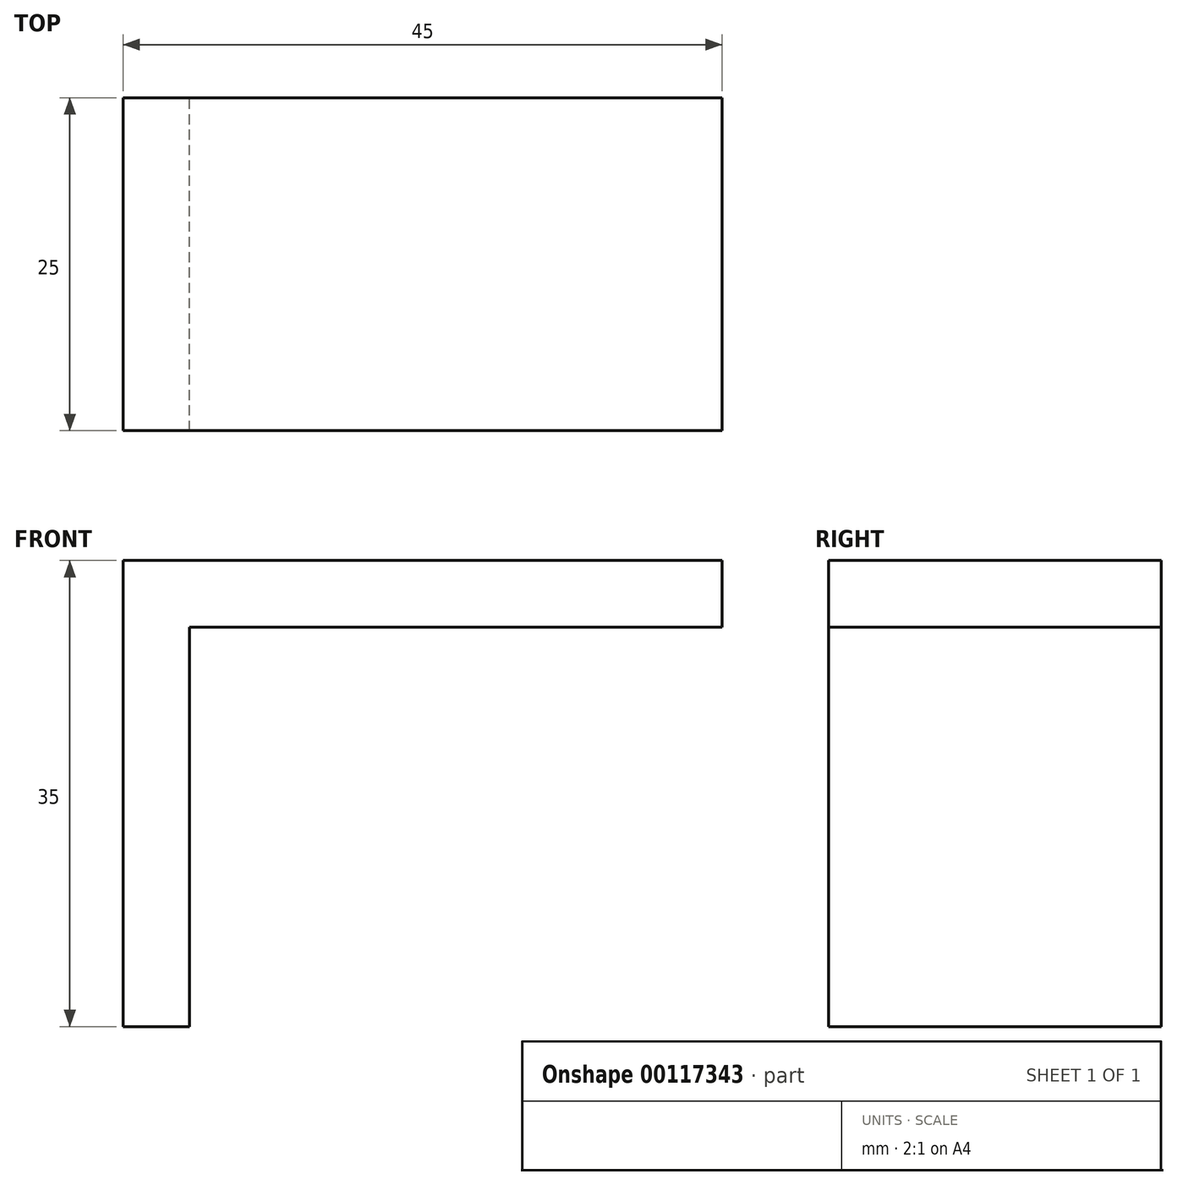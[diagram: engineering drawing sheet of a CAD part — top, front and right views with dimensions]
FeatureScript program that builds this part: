
annotation { "Feature Type Name" : "Feature", "Feature Type Description" : "" }
export const myFeature = defineFeature(function(context is Context, id is Id, definition is map)
    precondition{}
    {
        {
            var Q0;
            Q0=qCreatedBy(makeId("Front.planeOp"),FACE);
            var sketch = newSketch(context, id + "F0", { "sketchPlane" : qUnion([Q0])});
            skLineSegment(sketch, "E0", {"start": v(0, 0) * mm, "end": v(5, 0) * mm});
            skLineSegment(sketch, "E1", {"start": v(5, 0) * mm, "end": v(5, 30) * mm});
            skLineSegment(sketch, "E2", {"start": v(5, 30) * mm, "end": v(45, 30) * mm});
            skLineSegment(sketch, "E3", {"start": v(0, 0) * mm, "end": v(0, 35) * mm});
            skLineSegment(sketch, "E4", {"start": v(0, 35) * mm, "end": v(45, 35) * mm});
            skLineSegment(sketch, "E5", {"start": v(45, 35) * mm, "end": v(45, 30) * mm});
            skSolve(sketch);
        }
        {
            var Q0;
            Q0 = qSketchRegion(id + "F0", true);
            extrude(context, id + "F1", {"entities" : qUnion([Q0]), "depth" : 25 * mm});
        }
    });
